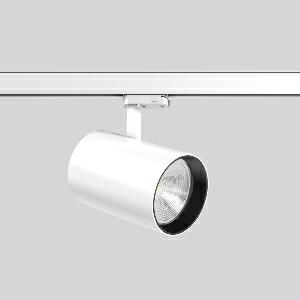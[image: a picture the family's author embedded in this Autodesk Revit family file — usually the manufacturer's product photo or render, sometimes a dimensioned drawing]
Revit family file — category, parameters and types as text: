
# Revit family: deecos_s_maxi_742218_002_bb4e
name_source: partatom
category: Lighting Fixtures
units: mm (PartAtom-declared; Revit-internal decimal feet)

## family parameters
Cut with Voids When Loaded = No
Host = Face
Light Source = No
Part Type = Normal
Room Calculation Point = No
Round Connector Dimension = Use Diameter
Shared = No

## types (1)
- DEECOS S maxi (1 x LED Modul 930, 2750 lm, 3000)
    Apparent Load = 25 VA
    Approval mark = CE
    CIE Flux Codes = 96 100 100 100 100
    Color Rendering = 90
    Color Temperature = 3000
    Default Elevation = 1800 mm
    Description = Series: DEECOS S maxi
LED surface-mounted projector in modern design with no visible cooling ribs. Housing: die-cast aluminium, powder-coated. Rotation range: 356°. Swivel range: 90°. Black plastic ring and recessed LED to prevent glare from the side. Optical assembly with lens made of plastic (polycarbonate) for the best homogeneous light distribution - can be changed without tools. Best colour rendering index Ra>90. With multi adaptor for 3-circuit tracks 230 V. Suitable for Track on ceiling, Wall track. High quality converter without flickering and stroboscopic effect. The following accessories can be mounted without use of tools: interchangeable lenses, decorative glasses, honeycomb louvre, clear and frosted diffusers, white interchangeable plastic ring. 
Colour: traffic white, matt (RAL 9016)
Diameter: 123 mm
Height: 200 mm
Lamp: LED
Socket: without socket
Colour temperature: 3000K
Colour rendering index (CRI): 92
System power: 25 W
Rated luminous flux: 2750 lm
Luminous efficiency: 110 lm/W
Control gear: Regulated power supply
Protection class: I
Type of protection: IP 20
    Height = 200 mm  [stored 0.656168 ft]
    Lamp = 1 x LED Modul 930
    Lamp Light Flux = 2750 lm
    Lamp count = 1
    Length = 123 mm
    Lifetime = 50000 h
    Luminous efficacy = 110 lm/W
    Manufacturer = RZB
    ModVariant = No
    Model = 742218.002
    Mounting Place = Ceiling
    Mounting Type = Rail mounted
    Number of Poles = 1
    OnlyDefault = Yes
    Power Factor = 1
    Product Name = DEECOS S maxi
    Product group = Track mounted projectors
    ProductGroupID = 301
    Protection Class = Protection class I
    Protection Degree = IP 20
    RLX_Detail_Level = 1
    RLX_Emergency_Light_Flux = 0 lm
    RLX_Emergency_Type = 0
    RLX_Emergency_Type_DB = No
    RlxData = <blob elided: 39541 chars, md5=8f750f9c>
    Socket = socket
    Standby Power = 0 W
    System Light Flux = 2750 lm
    System Power = 25 W
    Type Comments = Product without accessories
    Type Image = 741958.002.jpg
    URL = http://relux.com
    VarID = ---
    Voltage = 230 V
    Voltage Range = 220-240 V
    Weight = 0.00 kg
    Width = 0 mm  [stored 0 ft]

note: [stored X ft] marks values corroborated as IEEE doubles in the binary element streams (Revit-internal decimal feet)

## geometry (parser evidence)
native form markers: Blend x4, Sweep x13
no freeform markers — native parametric forms only
